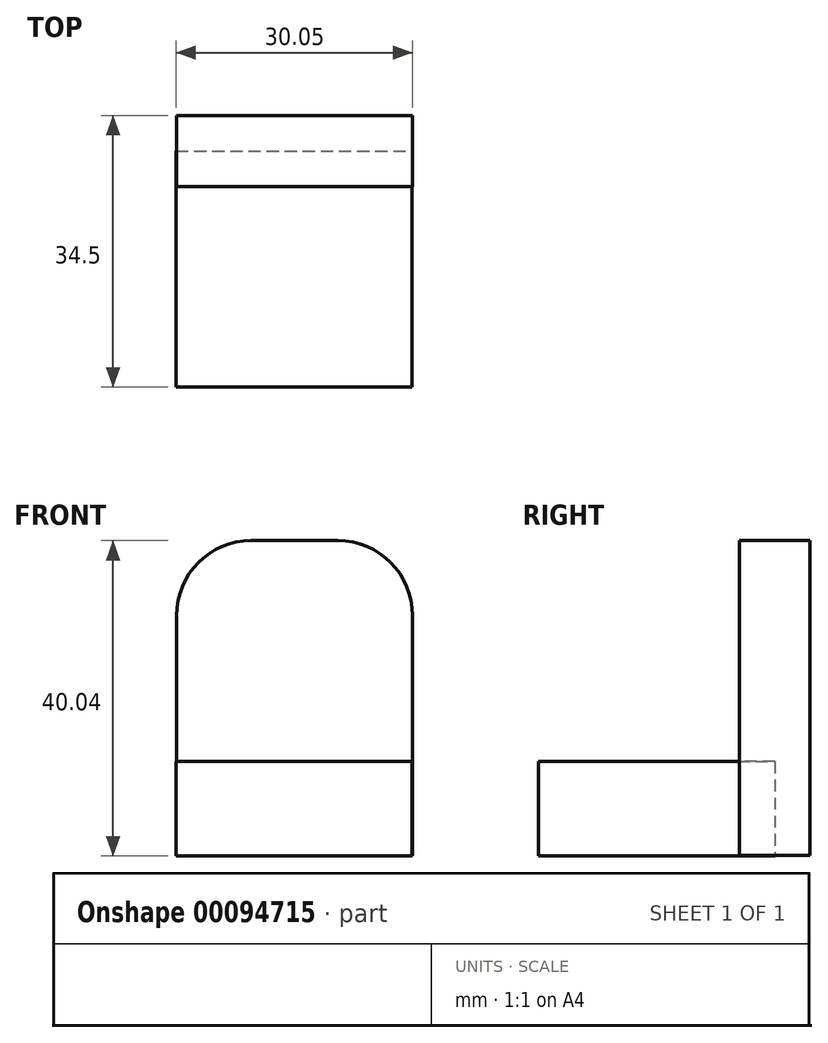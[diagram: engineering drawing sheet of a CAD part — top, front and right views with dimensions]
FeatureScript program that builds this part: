
annotation { "Feature Type Name" : "Feature", "Feature Type Description" : "" }
export const myFeature = defineFeature(function(context is Context, id is Id, definition is map)
    precondition{}
    {
        {
            var Q0;
            Q0=qCreatedBy(makeId("Front.planeOp"),FACE);
            var sketch = newSketch(context, id + "F0", { "sketchPlane" : qUnion([Q0])});
            skLineSegment(sketch, "E0.bottom", {"start": v(-2.4, 24.45) * mm, "end": v(8.6, 24.45) * mm});
            skLineSegment(sketch, "E0.top", {"start": v(-11.9, -15.55) * mm, "end": v(18.1, -15.55) * mm});
            skLineSegment(sketch, "E0.left", {"start": v(-11.9, 14.95) * mm, "end": v(-11.9, -15.55) * mm});
            skLineSegment(sketch, "E0.right", {"start": v(18.1, 14.95) * mm, "end": v(18.1, -15.55) * mm});
            skLineSegment(sketch, "E1", {"start": v(-11.9, -3.55) * mm, "end": v(18.1, -3.55) * mm});
            skPoint(sketch, "E2.visualSharp", {"position": v(18.1, 24.45) * mm});
            skArc(sketch, "E2.filletArc", {"start": v(18.1, 14.95) * mm, "mid": v(15.32, 21.67) * mm, "end": v(8.6, 24.45) * mm});
            skPoint(sketch, "E3.visualSharp", {"position": v(-11.9, 24.45) * mm});
            skArc(sketch, "E3.filletArc", {"start": v(-2.4, 24.45) * mm, "mid": v(-9.11, 21.67) * mm, "end": v(-11.9, 14.95) * mm});
            skPoint(sketch, "E4.centerSnap0", {"position": v(3.1, 24.45) * mm});
            skLineSegment(sketch, "E5.left", {"start": v(-11.9, -3.55) * mm, "end": v(-11.9, -15.55) * mm});
            skLineSegment(sketch, "E5.right", {"start": v(18.1, -3.55) * mm, "end": v(18.1, -15.55) * mm});
            skSolve(sketch);
        }
        {
            var Q0;
            Q0 = qSketchRegion(id + "F0", true);
            extrude(context, id + "F1", {"entities" : qUnion([Q0]), "endBound" : BoundingType.SYMMETRIC, "depth" : 9 * mm});
        }
        {
            var Q0;
            Q0=qCreatedBy(makeId("Front.planeOp"),FACE);
            var sketch = newSketch(context, id + "F2", { "sketchPlane" : qUnion([Q0])});
            skLineSegment(sketch, "E6.bottom", {"start": v(-11.95, -3.6) * mm, "end": v(18.05, -3.6) * mm});
            skLineSegment(sketch, "E6.top", {"start": v(-11.95, -15.6) * mm, "end": v(18.05, -15.6) * mm});
            skLineSegment(sketch, "E6.left", {"start": v(-11.95, -3.6) * mm, "end": v(-11.95, -15.6) * mm});
            skLineSegment(sketch, "E6.right", {"start": v(18.05, -3.6) * mm, "end": v(18.05, -15.6) * mm});
            skSolve(sketch);
        }
        {
            var Q0;
            Q0 = qSketchRegion(id + "F2", true);
            extrude(context, id + "F3", {"entities" : qUnion([Q0]), "operationType" : NewBodyOperationType.ADD, "depth" : 30 * mm});
        }
    });
